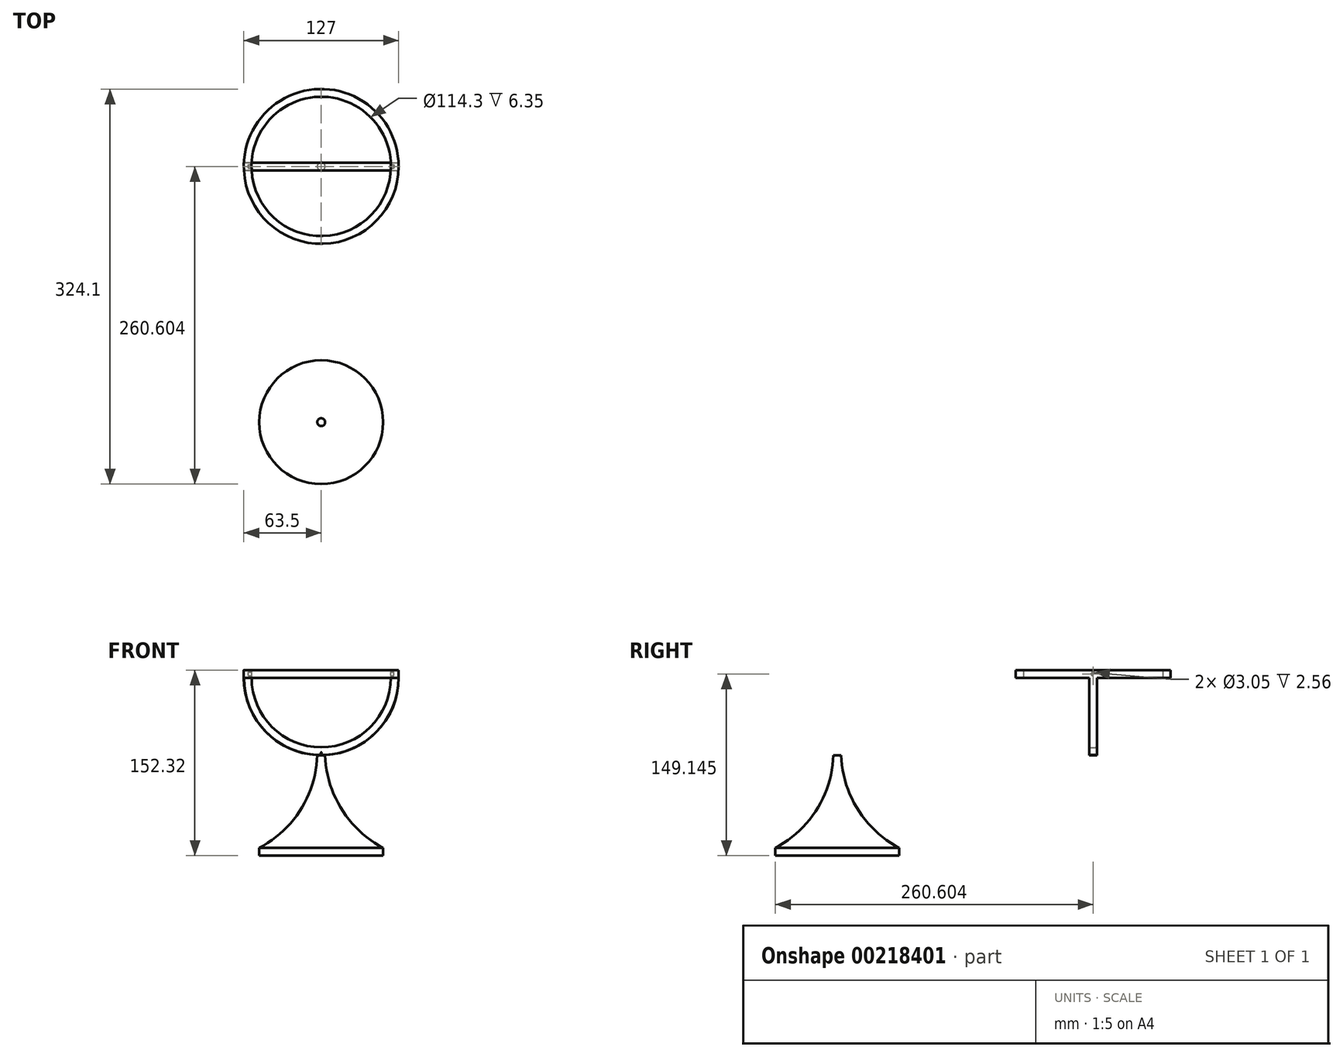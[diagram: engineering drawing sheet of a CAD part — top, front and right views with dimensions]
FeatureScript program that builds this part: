
annotation { "Feature Type Name" : "Feature", "Feature Type Description" : "" }
export const myFeature = defineFeature(function(context is Context, id is Id, definition is map)
    precondition{}
    {
        {
            var Q0;
            Q0=qCreatedBy(makeId("Top.planeOp"),FACE);
            var sketch = newSketch(context, id + "F0", { "sketchPlane" : qUnion([Q0])});
            skCircle(sketch, "E0", {"center": v(0, 0) * mm, "radius": 63.5 * mm});
            skCircle(sketch, "E1", {"center": v(0, 0) * mm, "radius": 57.15 * mm});
            skSolve(sketch);
        }
        {
            var Q0;
            Q0 = qSketchRegion(id + "F0", true);
            extrude(context, id + "F1", {"entities" : qUnion([Q0]), "depth" : 6.35 * mm});
        }
        {
            var Q0;
            Q0=makeQuery(id+"F1.opExtrude","CAP_FACE",FACE,{"disambiguationData":[OSD([sQuery(id+"F0.wireOp",EDGE,"E0"),sQuery(id+"F0.wireOp",EDGE,"E1")])],"isStart":true});
            var sketch = newSketch(context, id + "F2", { "sketchPlane" : qUnion([Q0])});
            skLineSegment(sketch, "E2", {"start": v(57.06, 3.18) * mm, "end": v(63.42, 3.18) * mm});
            skLineSegment(sketch, "E3", {"start": v(57.06, -3.18) * mm, "end": v(63.42, -3.18) * mm});
            skArc(sketch, "E4", {"start": v(57.06, -3.17) * mm, "mid": v(57.15, 0) * mm, "end": v(57.06, 3.17) * mm});
            skArc(sketch, "E5", {"start": v(63.42, 3.18) * mm, "mid": v(63.5, 0) * mm, "end": v(63.42, -3.17) * mm});
            skLineSegment(sketch, "E6", {"start": v(0, 11.02) * mm, "end": v(0, 0) * mm, "construction": true});
            skSolve(sketch);
        }
        {
            var Q0;
            Q0=makeQuery(id+"F2.imprint","IMPRINT",FACE,{"disambiguationData":[TD([[makeQuery(id+"F2.imprint","IMPRINT",EDGE,{"derivedFrom":sQuery(id+"F2.wireOp",EDGE,"E2")}),-1.0]])]});
            var Q1;
            Q1=sQuery(id+"F2.wireOp",EDGE,"E6");
            revolve(context, id + "F3", {"operationType" : NewBodyOperationType.ADD, "entities" : qUnion([Q0]), "axis" : qUnion([Q1]), "revolveType" : RevolveType.ONE_DIRECTION, "angle" : 180 * degree});
        }
        {
            var Q0;
            Q0=qCreatedBy(makeId("Front.planeOp"),FACE);
            var sketch = newSketch(context, id + "F4", { "sketchPlane" : qUnion([Q0])});
            skLineSegment(sketch, "E7", {"start": v(0, -63.42) * mm, "end": v(0, -139.62) * mm, "construction": true});
            skLineSegment(sketch, "E8", {"start": v(0, -139.62) * mm, "end": v(50.8, -139.62) * mm, "construction": true});
            skLineSegment(sketch, "E9", {"start": v(0, -63.42) * mm, "end": v(0, -60.88) * mm, "construction": true});
            skLineSegment(sketch, "E10", {"start": v(0, -60.88) * mm, "end": v(3.18, -60.88) * mm, "construction": true});
            skArc(sketch, "E11", {"start": v(3.17, -60.88) * mm, "mid": v(16.11, -106.83) * mm, "end": v(50.8, -139.62) * mm});
            skLineSegment(sketch, "E12", {"start": v(50.8, -139.62) * mm, "end": v(50.8, -145.97) * mm});
            skLineSegment(sketch, "E13", {"start": v(50.8, -145.97) * mm, "end": v(0, -145.97) * mm});
            skLineSegment(sketch, "E14", {"start": v(0, -145.97) * mm, "end": v(0, -60.88) * mm});
            skLineSegment(sketch, "E15", {"start": v(3.17, -60.88) * mm, "end": v(0, -60.88) * mm});
            skSolve(sketch);
        }
        {
            var Q0;
            Q0=makeQuery(id+"F4.imprint","IMPRINT",FACE,{"disambiguationData":[TD([[makeQuery(id+"F4.imprint","IMPRINT",EDGE,{"derivedFrom":sQuery(id+"F4.wireOp",EDGE,"E11")}),-1.0]])]});
            var Q1;
            Q1=sQuery(id+"F4.wireOp",EDGE,"E14");
            revolve(context, id + "F5", {"operationType" : NewBodyOperationType.ADD, "entities" : qUnion([Q0]), "axis" : qUnion([Q1]), "revolveType" : RevolveType.FULL});
        }
        {
            var Q0;
            Q0=qCreatedBy(makeId("Right.planeOp"),FACE);
            var sketch = newSketch(context, id + "F6", { "sketchPlane" : qUnion([Q0])});
            skLineSegment(sketch, "E16", {"start": v(0, 0) * mm, "end": v(0, 3.17) * mm, "construction": true});
            skCircle(sketch, "E17", {"center": v(0, 3.17) * mm, "radius": 1.52 * mm});
            skSolve(sketch);
        }
        {
            var Q0;
            Q0 = qSketchRegion(id + "F6", true);
            extrude(context, id + "F7", {"entities" : qUnion([Q0]), "operationType" : NewBodyOperationType.REMOVE, "oppositeDirection" : true, "depth" : 59.69 * mm, "hasSecondDirection" : true, "secondDirectionOppositeDirection" : false, "secondDirectionDepth" : 59.69 * mm});
        }
        {
            var Q0;
            Q0=makeQuery(id+"F1.opExtrude","SWEPT_BODY",BODY,{"disambiguationData":[OSD([sQuery(id+"F0.wireOp",EDGE,"E0"),sQuery(id+"F0.wireOp",EDGE,"E1")])]});
            transform(context, id + "F8", {"entities" : qUnion([Q0]), "transformType" : TransformType.TRANSLATION_3D, "dx" : 0 * mm, "dy" : 209.8 * mm, "dz" : 0 * mm, "makeCopy" : true});
        }
        {
            var Q0;
            Q0=qCreatedBy(makeId("Top.planeOp"),FACE);
            var sketch = newSketch(context, id + "F9", { "sketchPlane" : qUnion([Q0])});
            skCircle(sketch, "E18", {"center": v(0, 0) * mm, "radius": 79.89 * mm});
            skSolve(sketch);
        }
        {
            var Q0;
            Q0 = qSketchRegion(id + "F9", true);
            extrude(context, id + "F10", {"entities" : qUnion([Q0]), "operationType" : NewBodyOperationType.REMOVE, "oppositeDirection" : true, "depth" : 63.5 * mm, "hasSecondDirection" : true, "secondDirectionBound" : SecondDirectionBoundingType.THROUGH_ALL, "secondDirectionOppositeDirection" : false, "secondDirectionDepth" : 25.4 * mm});
        }
        {
            var Q0;
            Q0=makeQuery(id+"F10.boolean.opBoolean","COPY",FACE,{"derivedFrom":makeQuery(id+"F10.opExtrude","CAP_FACE",FACE,{"disambiguationData":[OSD([sQuery(id+"F9.wireOp",EDGE,"E18")])],"isStart":false})});
            var sketch = newSketch(context, id + "F11", { "sketchPlane" : qUnion([Q0])});
            skCircle(sketch, "E19", {"center": v(0, 208.75) * mm, "radius": 96.98 * mm});
            skSolve(sketch);
        }
        {
            var Q0;
            Q0 = qSketchRegion(id + "F11", true);
            extrude(context, id + "F12", {"entities" : qUnion([Q0]), "operationType" : NewBodyOperationType.REMOVE, "endBound" : BoundingType.THROUGH_ALL, "oppositeDirection" : true, "depth" : 102.36 * mm});
        }
    });
